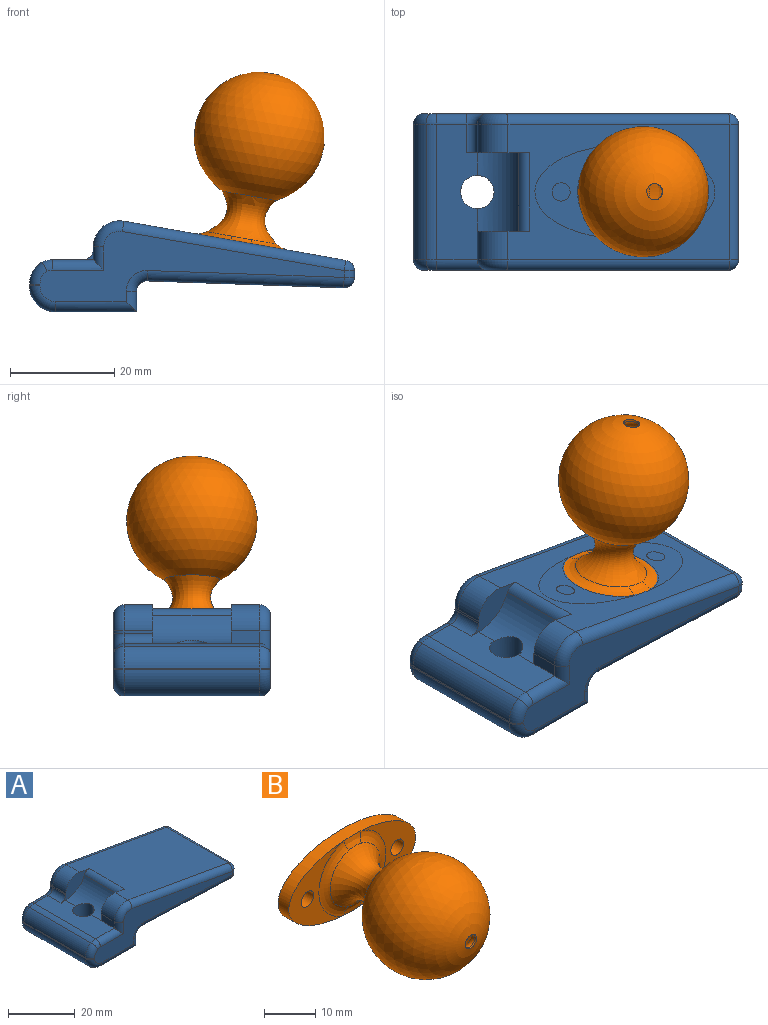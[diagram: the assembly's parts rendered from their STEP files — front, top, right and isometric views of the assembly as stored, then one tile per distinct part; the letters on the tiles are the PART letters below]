
ASSEMBLY  parts=2 mates=1
PART A: 56 faces, bbox 62.6x30x18.3 mm
  f0: plane 58.23x13.44mm, normal (0,1,0), area 309.3mm2, adj f20,f21,f23,f24,f25,f26,f27,f28
  f1: plane 5.5x0.44mm, normal (-1,0,0), area 2.4mm2, adj f13,f15,f22,f27
  f2: cylinder r=3.2mm len=10.63mm, axis (0,0,-1), area 204.2mm2, adj f5,f7,f14
  f3: plane 5.5x2.44mm, normal (-1,0,0), area 13.4mm2, adj f5,f12,f19,f50
  f4: plane 42.48x26mm, normal (0.17,0,0.98), area 1057.8mm2, adj f12,f13,f15,f19,f33,f41,f46,f55
  f5: plane 26x7.77mm, normal (0,0,1), area 174.9mm2, adj f2,f3,f13,f14,f17,f22,f23,f52
  f6: plane 26x0.28mm, normal (-1,0,0), area 7.4mm2, adj f16,f18,f24,f51
  f7: plane 26x15.5mm, normal (0,0,-1), area 370.8mm2, adj f2,f8,f18,f28,f47
  f8: plane 26x3.94mm, normal (1,0,0), area 102.3mm2, adj f7,f32,f40,f45
  f9: plane 37.59x26mm, normal (-0.03,0,-1), area 977.9mm2, adj f31,f35,f39,f40
  f10: plane 26x1.28mm, normal (1,0,0), area 33.4mm2, adj f34,f35,f41,f42
  f11: plane 58.23x13.44mm, normal (0,-1,0), area 305.9mm2, adj f39,f42,f43,f45,f46,f47,f48,f49
  f12: plane 10.05x7.44mm, normal (0,1,0), area 41.9mm2, adj f3,f4,f14,f19,f55
  f13: plane 12.05x7.44mm, normal (0,-1,0), area 42.8mm2, adj f1,f4,f5,f14,f15,f22,f55
  f14: cylinder r=8.4mm len=15mm, axis (0,1,0), area 135.2mm2, adj f2,f5,f12,f13,f55
  f15: cylinder r=5mm len=5.87mm, axis (0,-1,0), area 48mm2, adj f1,f4,f13,f29
  f16: cylinder r=5mm len=26mm, axis (0,1,0), area 133.4mm2, adj f6,f17,f21,f53
  f17: cylinder r=5mm len=26mm, axis (0,-1,0), area 54.9mm2, adj f5,f16,f20,f54
  f18: cylinder r=5mm len=26mm, axis (0,-1,0), area 204.2mm2, adj f6,f7,f26,f49
  f19: cylinder r=5mm len=5.87mm, axis (0,-1,0), area 48mm2, adj f3,f4,f12,f48
  f20: torus R=3mm, axis (0,-1,0), area 5.5mm2, adj f0,f17,f21,f23
  f21: torus R=3mm, axis (0,-1,0), area 13.6mm2, adj f0,f16,f20,f24
  f22: cylinder r=2mm len=5.5mm, axis (0,1,0), area 17.3mm2, adj f1,f5,f13,f25
  f23: cylinder r=2mm len=5.77mm, axis (-1,0,0), area 18.1mm2, adj f0,f5,f20,f25
  f24: cylinder r=2mm len=2mm, axis (0,0,-1), area 0.9mm2, adj f0,f6,f21,f26
  f25: torus R=4mm, axis (0,-1,0), area 13.5mm2, adj f0,f22,f23,f27
  f26: torus R=3mm, axis (0,-1,0), area 21.1mm2, adj f0,f18,f24,f28
  f27: cylinder r=2mm len=2mm, axis (0,0,-1), area 1.4mm2, adj f0,f1,f25,f29
  f28: cylinder r=2mm len=15.5mm, axis (1,0,0), area 46.4mm2, adj f0,f7,f26,f32
  f29: torus R=3mm, axis (0,-1,0), area 23.4mm2, adj f0,f15,f27,f33
  f30: sphere r=2mm, area 6.4mm2, adj f31,f34,f35
  f31: cylinder r=2mm len=37.66mm, axis (1,0,-0.03), area 118.2mm2, adj f0,f9,f30,f36
  f32: cylinder r=2mm len=3.94mm, axis (0,0,1), area 10.1mm2, adj f0,f8,f28,f36
  f33: cylinder r=2mm len=42.83mm, axis (-0.98,0,0.17), area 135.5mm2, adj f0,f4,f29,f37
  f34: cylinder r=2mm len=2mm, axis (0,0,1), area 4mm2, adj f0,f10,f30,f37
  f35: cylinder r=2mm len=26mm, axis (0,1,0), area 83.5mm2, adj f9,f10,f30,f38
  f36: torus R=4mm, axis (0,-1,0), area 13.8mm2, adj f0,f31,f32,f40
  f37: sphere r=2mm, area 5.6mm2, adj f33,f34,f41
  f38: sphere r=2mm, area 6.4mm2, adj f35,f39,f42
  f39: cylinder r=2mm len=37.66mm, axis (-1,0,0.03), area 118.2mm2, adj f9,f11,f38,f43
  f40: cylinder r=2mm len=26mm, axis (0,1,0), area 83.5mm2, adj f8,f9,f36,f43
  f41: cylinder r=2mm len=26mm, axis (0,1,0), area 72.6mm2, adj f4,f10,f37,f44
  f42: cylinder r=2mm len=2mm, axis (0,0,-1), area 4mm2, adj f10,f11,f38,f44
  f43: torus R=4mm, axis (0,-1,0), area 13.8mm2, adj f11,f39,f40,f45
  f44: sphere r=2mm, area 5.6mm2, adj f41,f42,f46
  f45: cylinder r=2mm len=3.94mm, axis (0,0,-1), area 10.1mm2, adj f8,f11,f43,f47
  f46: cylinder r=2mm len=42.83mm, axis (0.98,0,-0.17), area 135.5mm2, adj f4,f11,f44,f48
  f47: cylinder r=2mm len=15.5mm, axis (-1,0,0), area 46.4mm2, adj f7,f11,f45,f49
  f48: torus R=3mm, axis (0,-1,0), area 23.4mm2, adj f11,f19,f46,f50
  f49: torus R=3mm, axis (0,-1,0), area 21.1mm2, adj f11,f18,f47,f51
  f50: cylinder r=2mm len=4.44mm, axis (0,0,1), area 10mm2, adj f3,f11,f48,f52
  f51: cylinder r=2mm len=2mm, axis (0,0,1), area 0.9mm2, adj f6,f11,f49,f53
  f52: cylinder r=2mm len=9.77mm, axis (1,0,0), area 26.7mm2, adj f5,f11,f50,f54
  f53: torus R=3mm, axis (0,-1,0), area 13.6mm2, adj f11,f16,f51,f54
  f54: torus R=3mm, axis (0,-1,0), area 5.5mm2, adj f11,f17,f52,f53
  f55: cylinder r=2mm len=15mm, axis (0,1,0), area 41.3mm2, adj f4,f12,f13,f14
PART B: 17 faces, bbox 35x36.7x25 mm
  f0: plane 17.83x15.11mm, normal (0,-1,0), area 104.7mm2, adj f3,f4,f13
  f1: cylinder r=1.75mm len=3.5mm, axis (0,-1,0), area 33mm2, adj f5,f6
  f2: cylinder r=1.55mm len=11.36mm, axis (0,-1,0), area 110.6mm2, adj f5,f15
  f3: extruded ~35x18mm, area 256.2mm2, adj f0,f5,f6,f11,f14
  f4: cylinder r=1.75mm len=3.5mm, axis (0,-1,0), area 33mm2, adj f0,f5
  f5: plane 35x18mm, normal (0,1,0), area 468mm2, adj f1,f2,f3,f4
  f6: plane 17.83x15.11mm, normal (0,-1,0), area 104.7mm2, adj f1,f3,f12
  f7: sphere r=10.5mm, area 1328.4mm2, adj f15,f16
  f8: cylinder r=1.55mm len=3.1mm, axis (0,1,0), area 4.1mm2, adj f9,f16
  f9: sphere r=12.5mm, area 1865.1mm2, adj f8,f10
  f10: revolved ~13.69x13.68mm, area 286.9mm2, adj f9,f11,f12,f13,f14
  f11: bspline ~6.82x2.69mm, area 5.1mm2, adj f3,f10,f12,f13
  f12: torus R=9.23mm, axis (0,1,0), area 53mm2, adj f6,f10,f11,f14
  f13: torus R=9.23mm, axis (0,1,0), area 53mm2, adj f0,f10,f11,f14
  f14: bspline ~6.82x2.69mm, area 9.8mm2, adj f3,f10,f12,f13
  f15: torus R=3.55mm, axis (0,-1,0), area 33.1mm2, adj f2,f7
  f16: torus R=3.55mm, axis (0,1,0), area 33.1mm2, adj f7,f8
PLACE A t=(-0.16,0,-0.9)mm
PLACE B rot(axis=(-0.99,0.09,0.09),90.4deg) t=(28.1,0,-5.89)mm
MATE slider B.f12 <-> A.f4  axis (-0.17,0,-0.98) through (28.22,0,-5.19)mm
